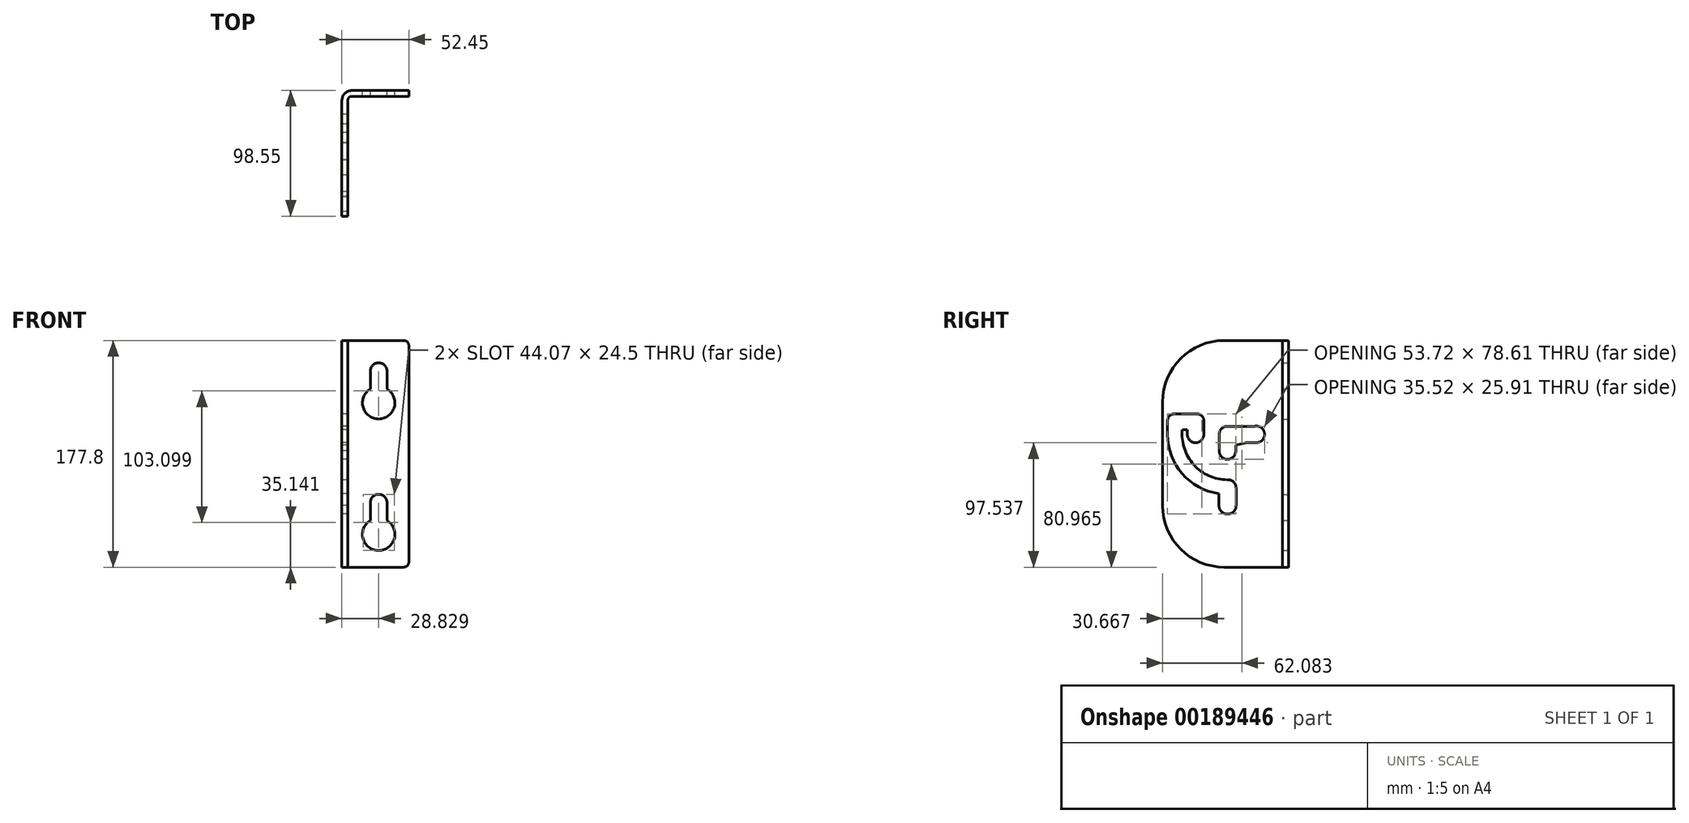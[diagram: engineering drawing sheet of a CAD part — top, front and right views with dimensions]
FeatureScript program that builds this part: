
annotation { "Feature Type Name" : "Feature", "Feature Type Description" : "" }
export const myFeature = defineFeature(function(context is Context, id is Id, definition is map)
    precondition{}
    {
        {
            var Q0;
            Q0=qCreatedBy(makeId("Top.planeOp"),FACE);
            var sketch = newSketch(context, id + "F0", { "sketchPlane" : qUnion([Q0])});
            skLineSegment(sketch, "E0", {"start": v(8, 0) * mm, "end": v(52.45, 0) * mm});
            skLineSegment(sketch, "E1", {"start": v(52.45, 0) * mm, "end": v(52.45, -4.78) * mm});
            skLineSegment(sketch, "E2", {"start": v(52.45, -4.78) * mm, "end": v(7.32, -4.78) * mm});
            skLineSegment(sketch, "E3", {"start": v(4.78, -7.32) * mm, "end": v(4.78, -98.55) * mm});
            skLineSegment(sketch, "E4", {"start": v(4.78, -98.55) * mm, "end": v(0, -98.55) * mm});
            skLineSegment(sketch, "E5", {"start": v(0, -98.55) * mm, "end": v(0, -8) * mm});
            skPoint(sketch, "E6.visualSharp", {"position": v(0, 0) * mm});
            skArc(sketch, "E6.filletArc", {"start": v(8, 0) * mm, "mid": v(2.34, -2.34) * mm, "end": v(0, -8) * mm});
            skPoint(sketch, "E7.visualSharp", {"position": v(4.78, -4.78) * mm});
            skArc(sketch, "E7.filletArc", {"start": v(7.32, -4.78) * mm, "mid": v(5.52, -5.52) * mm, "end": v(4.78, -7.32) * mm});
            skSolve(sketch);
        }
        {
            var Q0;
            Q0 = qSketchRegion(id + "F0", true);
            extrude(context, id + "F1", {"entities" : qUnion([Q0]), "depth" : 177.8 * mm});
        }
        {
            var Q0;
            Q0=makeQuery(id+"F1.opExtrude","SWEPT_FACE",FACE,{"disambiguationData":[OSD([sQuery(id+"F0.wireOp",EDGE,"E0")])]});
            var sketch = newSketch(context, id + "F2", { "sketchPlane" : qUnion([Q0])});
            skLineSegment(sketch, "E8", {"start": v(-48.39, 177.8) * mm, "end": v(-52.45, 177.8) * mm});
            skLineSegment(sketch, "E9", {"start": v(-52.45, 177.8) * mm, "end": v(-52.45, 173.74) * mm});
            skLineSegment(sketch, "E10", {"start": v(-52.45, 4.06) * mm, "end": v(-52.45, 0) * mm});
            skLineSegment(sketch, "E11", {"start": v(-52.45, 0) * mm, "end": v(-48.39, 0) * mm});
            skArc(sketch, "E12", {"start": v(-48.39, 177.8) * mm, "mid": v(-51.26, 176.6) * mm, "end": v(-52.45, 173.74) * mm});
            skArc(sketch, "E13", {"start": v(-52.45, 4.06) * mm, "mid": v(-51.26, 1.2) * mm, "end": v(-48.39, 0) * mm});
            skArc(sketch, "E14", {"start": v(-35.3, 36.73) * mm, "mid": v(-28.83, 13.1) * mm, "end": v(-22.35, 36.73) * mm});
            skArc(sketch, "E15", {"start": v(-22.35, 50.7) * mm, "mid": v(-28.83, 57.18) * mm, "end": v(-35.3, 50.7) * mm});
            skLineSegment(sketch, "E16", {"start": v(-28.83, 50.7) * mm, "end": v(-28.83, 25.8) * mm});
            skLineSegment(sketch, "E17", {"start": v(-52.45, 25.8) * mm, "end": v(-28.83, 25.8) * mm});
            skLineSegment(sketch, "E18", {"start": v(-35.3, 50.7) * mm, "end": v(-35.3, 36.73) * mm});
            skLineSegment(sketch, "E19", {"start": v(-22.35, 36.73) * mm, "end": v(-22.35, 50.7) * mm});
            skArc(sketch, "E20", {"start": v(-35.3, 139.83) * mm, "mid": v(-28.83, 116.2) * mm, "end": v(-22.35, 139.83) * mm});
            skArc(sketch, "E21", {"start": v(-22.35, 153.8) * mm, "mid": v(-28.83, 160.27) * mm, "end": v(-35.3, 153.8) * mm});
            skLineSegment(sketch, "E22", {"start": v(-28.83, 153.8) * mm, "end": v(-28.83, 128.9) * mm});
            skLineSegment(sketch, "E23", {"start": v(-65.05, 128.9) * mm, "end": v(-28.83, 128.9) * mm});
            skLineSegment(sketch, "E24", {"start": v(-35.3, 153.8) * mm, "end": v(-35.3, 139.83) * mm});
            skLineSegment(sketch, "E25", {"start": v(-22.35, 139.83) * mm, "end": v(-22.35, 153.8) * mm});
            skSolve(sketch);
        }
        {
            var Q0;
            Q0 = qSketchRegion(id + "F2", true);
            extrude(context, id + "F3", {"entities" : qUnion([Q0]), "operationType" : NewBodyOperationType.REMOVE, "endBound" : BoundingType.THROUGH_ALL, "oppositeDirection" : true, "depth" : 25.4 * mm});
        }
        {
            var Q0;
            Q0=makeQuery(id+"F1.opExtrude","SWEPT_FACE",FACE,{"disambiguationData":[OSD([sQuery(id+"F0.wireOp",EDGE,"E5")])]});
            var sketch = newSketch(context, id + "F4", { "sketchPlane" : qUnion([Q0])});
            skLineSegment(sketch, "E26", {"start": v(94.74, 100.5) * mm, "end": v(94.74, 114.94) * mm});
            skLineSegment(sketch, "E27", {"start": v(89.4, 120.27) * mm, "end": v(71.63, 120.27) * mm});
            skLineSegment(sketch, "E28", {"start": v(66.3, 114.94) * mm, "end": v(66.3, 104.14) * mm});
            skArc(sketch, "E29", {"start": v(66.3, 104.14) * mm, "mid": v(72.77, 97.66) * mm, "end": v(79.25, 104.14) * mm});
            skPoint(sketch, "E30.visualSharp", {"position": v(66.3, 120.27) * mm});
            skArc(sketch, "E30.filletArc", {"start": v(71.63, 120.27) * mm, "mid": v(67.86, 118.7) * mm, "end": v(66.3, 114.94) * mm});
            skPoint(sketch, "E31.visualSharp", {"position": v(94.74, 120.27) * mm});
            skArc(sketch, "E31.filletArc", {"start": v(94.74, 114.94) * mm, "mid": v(93.18, 118.7) * mm, "end": v(89.4, 120.27) * mm});
            skLineSegment(sketch, "E32", {"start": v(72.77, 104.14) * mm, "end": v(79.25, 104.14) * mm});
            skArc(sketch, "E33", {"start": v(47.75, 68.58) * mm, "mid": v(74.2, 80.38) * mm, "end": v(83.1, 107.95) * mm});
            skArc(sketch, "E34", {"start": v(54.48, 57.64) * mm, "mid": v(87.89, 79.7) * mm, "end": v(92.16, 119.5) * mm});
            skArc(sketch, "E35", {"start": v(41.02, 48.56) * mm, "mid": v(47.67, 41.66) * mm, "end": v(54.48, 48.4) * mm});
            skLineSegment(sketch, "E36", {"start": v(47.75, 68.58) * mm, "end": v(47.37, 68.58) * mm});
            skLineSegment(sketch, "E37", {"start": v(41.02, 48.56) * mm, "end": v(41.02, 62.23) * mm});
            skLineSegment(sketch, "E38", {"start": v(54.48, 48.4) * mm, "end": v(54.48, 57.64) * mm});
            skLineSegment(sketch, "E39", {"start": v(79.25, 104.14) * mm, "end": v(79.25, 107.95) * mm});
            skLineSegment(sketch, "E40", {"start": v(79.25, 107.95) * mm, "end": v(83.1, 107.95) * mm});
            skPoint(sketch, "E41.orphan", {"position": v(83.31, 104.14) * mm});
            skArc(sketch, "E42.filletArc", {"start": v(47.37, 68.58) * mm, "mid": v(42.88, 66.72) * mm, "end": v(41.02, 62.23) * mm});
            skArc(sketch, "E43", {"start": v(41.28, 91.4) * mm, "mid": v(47.59, 84.58) * mm, "end": v(54.23, 91.06) * mm});
            skArc(sketch, "E44", {"start": v(26.42, 110.5) * mm, "mid": v(18.7, 104.82) * mm, "end": v(25.06, 97.66) * mm});
            skLineSegment(sketch, "E45", {"start": v(54.23, 91.06) * mm, "end": v(54.23, 104.14) * mm});
            skLineSegment(sketch, "E46", {"start": v(26.42, 110.5) * mm, "end": v(47.88, 110.5) * mm});
            skLineSegment(sketch, "E47", {"start": v(41.28, 91.4) * mm, "end": v(41.28, 95.74) * mm});
            skLineSegment(sketch, "E48", {"start": v(25.06, 97.66) * mm, "end": v(32.9, 97.56) * mm});
            skArc(sketch, "E49.filletArc", {"start": v(54.23, 104.14) * mm, "mid": v(52.37, 108.63) * mm, "end": v(47.88, 110.5) * mm});
            skLineSegment(sketch, "E50", {"start": v(32.9, 97.56) * mm, "end": v(41.28, 95.74) * mm});
            skLineSegment(sketch, "E51", {"start": v(98.55, 48.26) * mm, "end": v(98.55, 0) * mm});
            skLineSegment(sketch, "E52", {"start": v(50.3, 0) * mm, "end": v(98.55, 0) * mm});
            skLineSegment(sketch, "E53", {"start": v(50.3, 177.8) * mm, "end": v(98.55, 177.8) * mm});
            skLineSegment(sketch, "E54", {"start": v(98.55, 177.8) * mm, "end": v(98.55, 129.54) * mm});
            skArc(sketch, "E55", {"start": v(50.3, 0) * mm, "mid": v(84.42, 14.14) * mm, "end": v(98.55, 48.26) * mm});
            skArc(sketch, "E56.trimOffspring", {"start": v(98.55, 129.54) * mm, "mid": v(84.42, 163.66) * mm, "end": v(50.3, 177.8) * mm});
            skLineSegment(sketch, "E57", {"start": v(47.75, 104.14) * mm, "end": v(72.77, 104.14) * mm});
            skSolve(sketch);
        }
        {
            var Q0;
            Q0 = qSketchRegion(id + "F4", true);
            extrude(context, id + "F5", {"entities" : qUnion([Q0]), "operationType" : NewBodyOperationType.REMOVE, "endBound" : BoundingType.THROUGH_ALL, "oppositeDirection" : true, "depth" : 25.4 * mm});
        }
    });
